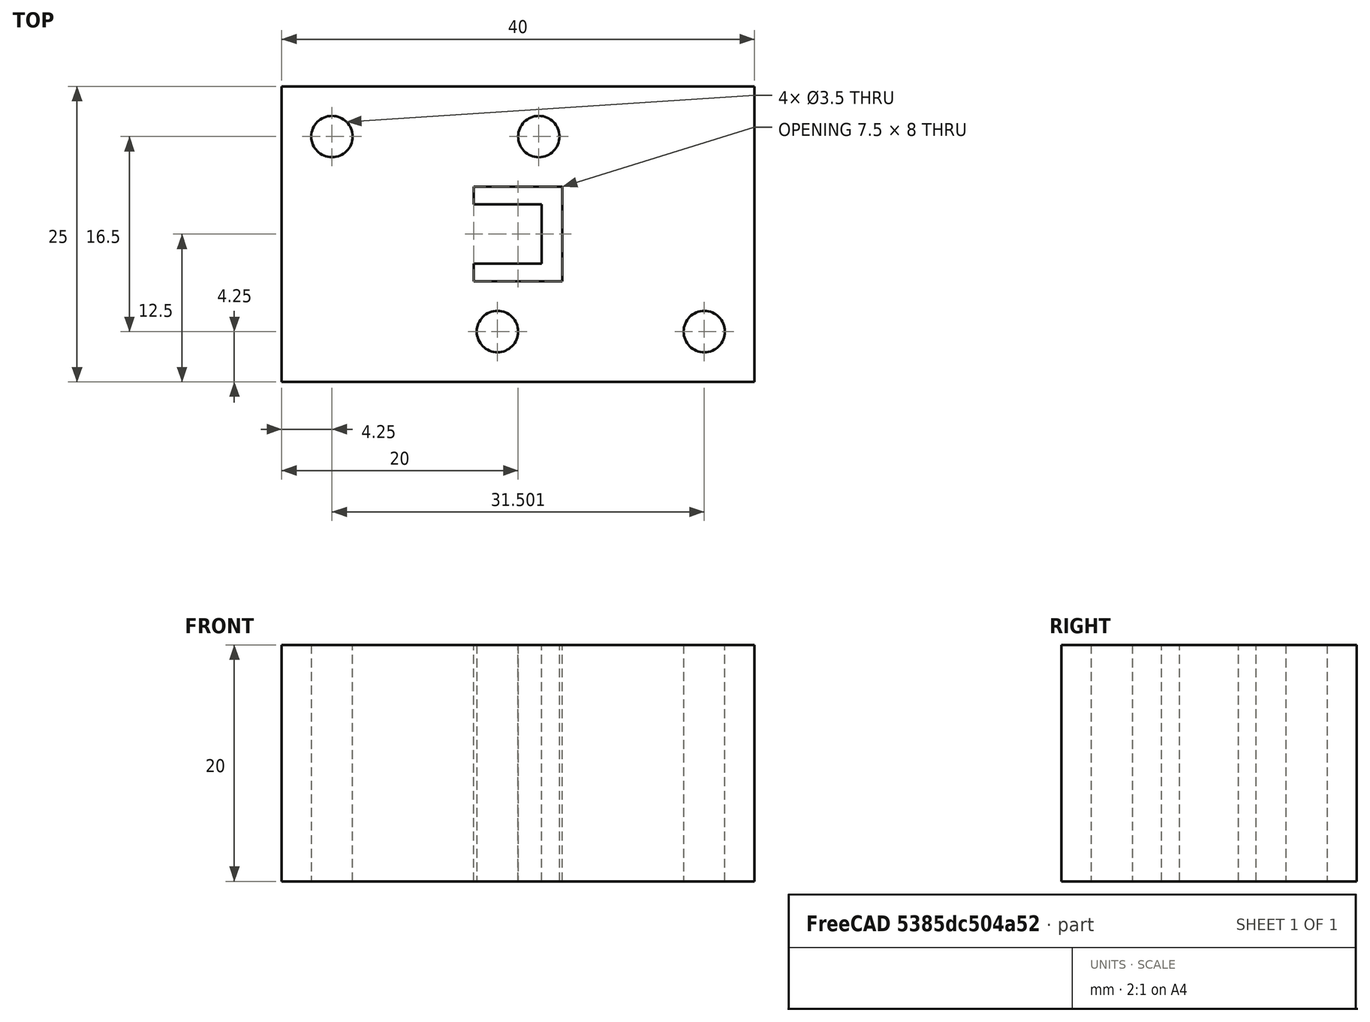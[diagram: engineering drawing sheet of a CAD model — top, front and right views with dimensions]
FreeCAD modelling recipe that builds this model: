
FCSTD DOCUMENT  (FreeCAD 0.21R33771 (Git))
Label: Vastmaakfinal
License: All rights reserved
LicenseURL: https://en.wikipedia.org/wiki/All_rights_reserved
objects: Sketcher::SketchObject×1, PartDesign::Pad×1, PartDesign::Body×1
note: 4 computed .brp shape members not serialized (recipe doc carries the construction recipe); baked Part::Feature solids carry a one-line shape summary decoded from their .brp

FEATURE [Sketcher::SketchObject] Sketch001
  FullyConstrained = true
  Placement = pos=(0,0,5) rot=(0,0,1;0rad)
  sketch-geometry (17):
    g0: LineSegment StartX=3.75 StartY=-4 StartZ=0 EndX=3.75 EndY=4 EndZ=0
    g1: LineSegment StartX=3.75 StartY=-4 StartZ=0 EndX=-3.75 EndY=-4 EndZ=0
    g2: LineSegment StartX=3.75 StartY=4 StartZ=0 EndX=-3.75 EndY=4 EndZ=0
    g3: LineSegment StartX=-3.75 StartY=4 StartZ=0 EndX=-3.75 EndY=2.5 EndZ=0
    g4: LineSegment StartX=-3.75 StartY=-4 StartZ=0 EndX=-3.75 EndY=-2.5 EndZ=0
    g5: LineSegment StartX=-3.75 StartY=-2.5 StartZ=0 EndX=2 EndY=-2.5 EndZ=0
    g6: LineSegment StartX=-3.75 StartY=2.5 StartZ=0 EndX=2 EndY=2.5 EndZ=0
    g7: LineSegment StartX=2 StartY=2.5 StartZ=0 EndX=2 EndY=-2.5 EndZ=0
    g8: LineSegment StartX=20 StartY=-12.5 StartZ=0 EndX=20 EndY=12.5 EndZ=0
    g9: LineSegment StartX=20 StartY=12.5 StartZ=0 EndX=-20 EndY=12.5 EndZ=0
    g10: LineSegment StartX=-20 StartY=12.5 StartZ=0 EndX=-20 EndY=-12.5 EndZ=0
    g11: LineSegment StartX=-20 StartY=-12.5 StartZ=0 EndX=20 EndY=-12.5 EndZ=0
    g12: GeomPoint X=0 Y=0 Z=0
    g13: Circle CenterX=-1.74617 CenterY=-8.24603 CenterZ=0 NormalX=0 NormalY=0 NormalZ=1 AngleXU=0 Radius=1.75
    g14: Circle CenterX=1.75212 CenterY=8.2493 CenterZ=0 NormalX=0 NormalY=0 NormalZ=1 AngleXU=0 Radius=1.75
    g15: Circle CenterX=15.7515 CenterY=-8.2499 CenterZ=0 NormalX=0 NormalY=0 NormalZ=1 AngleXU=0 Radius=1.75
    g16: Circle CenterX=-15.7497 CenterY=8.24974 CenterZ=0 NormalX=0 NormalY=0 NormalZ=1 AngleXU=0 Radius=1.75
  constraints (42):
    c: DistanceY(g0,g0) = 8
    c: Symmetric(g0,g0,g-1)
    c: Coincident(g1,g0)
    c: Coincident(g2,g0)
    c: Horizontal(g2)
    c: DistanceX(g2,g2) = 7.5
    c: DistanceX(g1,g1) = 7.5
    c: Symmetric(g1,g0,g-2)
    c: Coincident(g3,g2)
    c: Vertical(g3)
    c: Coincident(g4,g1)
    c: Vertical(g4)
    c: DistanceY(g4,g4) = 1.5
    c: DistanceY(g3,g3) = 1.5
    c: Coincident(g5,g4)
    c: Horizontal(g5)
    c: Coincident(g6,g3)
    c: Horizontal(g6)
    c: Coincident(g7,g6)
    c: Coincident(g7,g5)
    c: Vertical(g7)
    c: DistanceX(g6,g6) = 5.75
    c: Coincident(g8,g9)
    c: Coincident(g9,g10)
    c: Coincident(g10,g11)
    c: Coincident(g11,g8)
    c: Horizontal(g9)
    c: Horizontal(g11)
    c: Vertical(g8)
    c: Vertical(g10)
    c: Symmetric(g9,g8,g12)
    c: Coincident(g12,g-1)
    c: DistanceX(g9,g9) = 40
    c: DistanceY(g10,g10) = 25
    c: Radius(g13) = 1.75
    c: Radius(g14) = 1.75
    c: Block(g13)
    c: Block(g14)
    c: Radius(g15) = 1.75
    c: Block(g15)
    c: Radius(g16) = 1.75
    c: Block(g16)
FEATURE [PartDesign::Pad] Pad
  Direction = (0,0,1)
  Length = 20
  Length2 = 10
  Placement = pos=(0,0,5) rot=(0,0,1;0rad)
  Profile = -> Sketch001
  ReferenceAxis = -> Sketch001 [N_Axis]
  Type = 0
FEATURE [PartDesign::Body] Body001
  Group = -> [Sketch001,Pad]
  Origin = -> Origin001
  Tip = -> Pad
